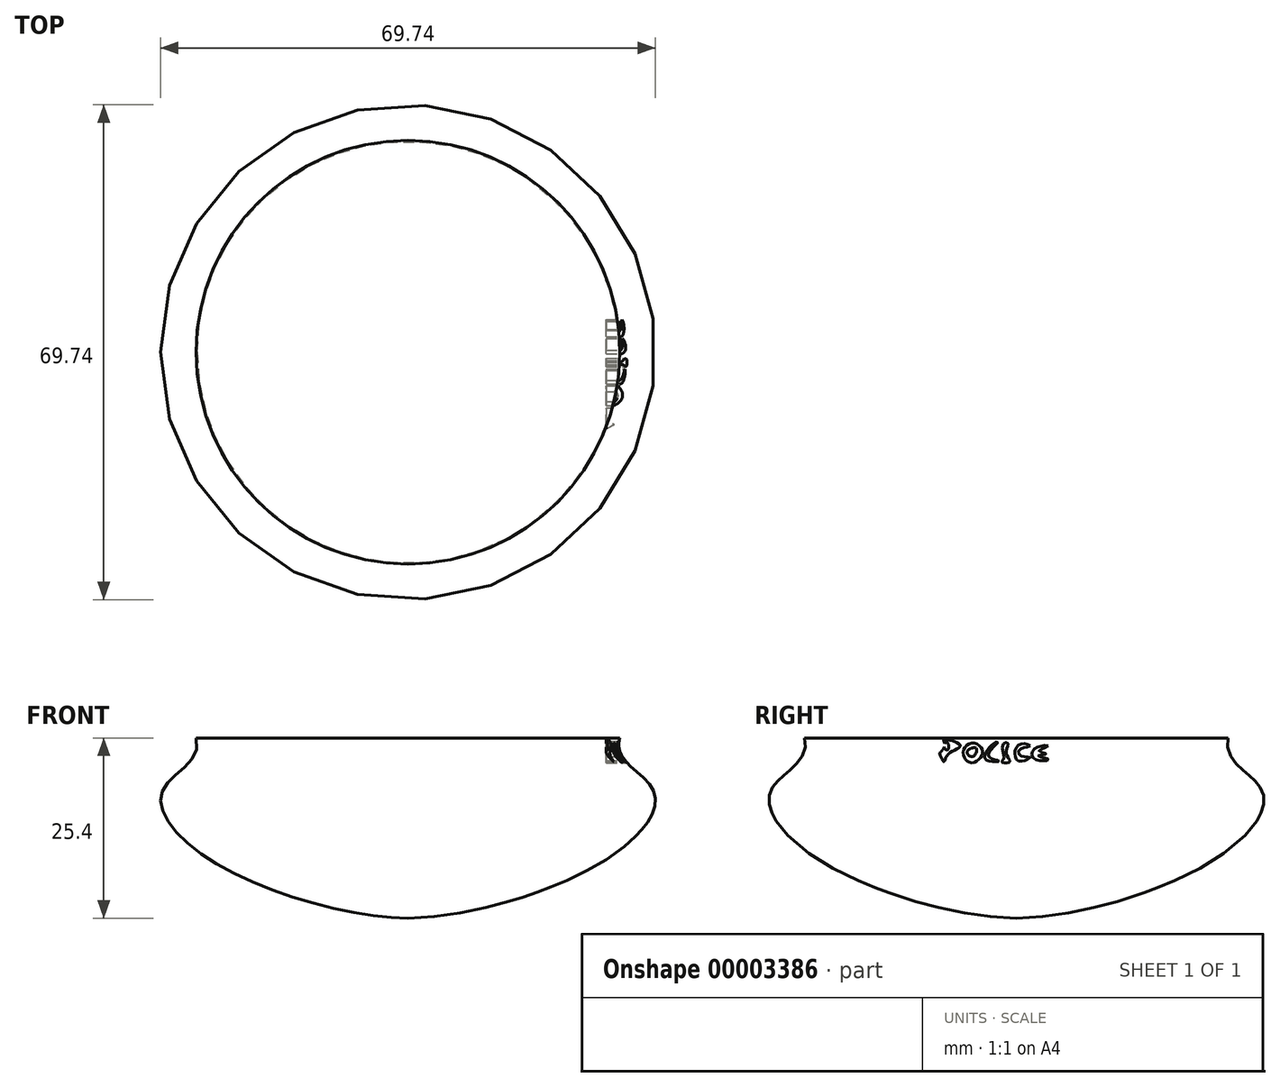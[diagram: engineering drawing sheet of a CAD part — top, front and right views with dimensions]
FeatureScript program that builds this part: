
annotation { "Feature Type Name" : "Feature", "Feature Type Description" : "" }
export const myFeature = defineFeature(function(context is Context, id is Id, definition is map)
    precondition{}
    {
        {
            var Q0;
            Q0=qCreatedBy(makeId("Front.planeOp"),FACE);
            var sketch = newSketch(context, id + "F0", { "sketchPlane" : qUnion([Q0])});
            skFitSpline(sketch, "E0", {"points": [v(-29.85, 0) * mm, v(-34.49, -7.2) * mm, v(-28.54, -16.76) * mm, v(0, -25.4) * mm], "startDerivative": vector(11.46, -40.51) * mm, "endDerivative": vector(51.25, -0.05) * mm});
            skLineSegment(sketch, "E1", {"start": v(-29.85, 0) * mm, "end": v(0, 0) * mm});
            skLineSegment(sketch, "E2", {"start": v(0, 0) * mm, "end": v(0, -25.4) * mm});
            skSolve(sketch);
        }
        {
            var Q0;
            Q0=qCreatedBy(makeId("Front.planeOp"),FACE);
            var sketch = newSketch(context, id + "F1", { "sketchPlane" : qUnion([Q0])});
            skLineSegment(sketch, "E3", {"start": v(0, 38.14) * mm, "end": v(0, -46.32) * mm});
            skSolve(sketch);
        }
        {
            var Q0;
            Q0=makeQuery(id+"F0.imprint","IMPRINT",FACE,{"disambiguationData":[TD([[makeQuery(id+"F0.imprint","IMPRINT",EDGE,{"derivedFrom":sQuery(id+"F0.wireOp",EDGE,"E0")}),1.0]])]});
            var Q1;
            {var subQ0=sQuery(id+"F0.wireOp",EDGE,"7daf59d7-36d5-40c3-b46c-32f78c155582");Q1=makeQuery(id+"F0.imprint","IMPRINT",FACE,{"disambiguationData":[TD([[makeQuery(id+"F0.imprint","IMPRINT",EDGE,{"derivedFrom":subQ0}),1.0]])]});}
            var Q2;
            {var subQ1=sQuery(id+"F0.wireOp",EDGE,"db690256-2e2c-4568-aae6-5ea2a57716da");Q2=makeQuery(id+"F0.imprint","IMPRINT",FACE,{"disambiguationData":[TD([[makeQuery(id+"F0.imprint","IMPRINT",EDGE,{"derivedFrom":subQ1}),1.0]])]});}
            var Q3;
            Q3=sQuery(id+"F1.wireOp",EDGE,"E3");
            revolve(context, id + "F2", {"entities" : qUnion([Q0, Q1, Q2]), "axis" : qUnion([Q3]), "revolveType" : RevolveType.FULL});
        }
        {
            var Q0;
            Q0=qCreatedBy(makeId("Right.planeOp"),FACE);
            cPlane(context, id + "F3", {"entities" : qUnion([Q0]), "cplaneType" : CPlaneType.OFFSET, "offset" : 27.94 * mm, "width" : 152.4 * mm, "height" : 152.4 * mm});
        }
        {
            var Q0;
            Q0=qCreatedBy(id+"F3.planeOp",FACE);
            var sketch = newSketch(context, id + "F4", { "sketchPlane" : qUnion([Q0])});
            skFitSpline(sketch, "E4", {"points": [v(-10.23, -3.34) * mm, v(-10.74, -0.55) * mm, v(-7.93, -1.06) * mm, v(-9.7, -2.4) * mm, v(-10.23, -3.34) * mm]});
            skFitSpline(sketch, "E5", {"points": [v(-10.23, -1) * mm, v(-9.7, -0.66) * mm, v(-9.7, -1.68) * mm, v(-10.23, -1) * mm]});
            skFitSpline(sketch, "E6", {"points": [v(-6.33, -3.5) * mm, v(-7.5, -2.04) * mm, v(-6.3, -0.72) * mm, v(-4.75, -1.9) * mm, v(-6.33, -3.5) * mm]});
            skFitSpline(sketch, "E7", {"points": [v(-6.55, -2.6) * mm, v(-6.93, -1.9) * mm, v(-5.7, -1.4) * mm, v(-5.85, -2.38) * mm, v(-6.55, -2.6) * mm]});
            skFitSpline(sketch, "E8", {"points": [v(-3.2, -0.77) * mm, v(-4.34, -3) * mm, v(-2.38, -3.26) * mm, v(-3.94, -2.54) * mm, v(-2.57, -0.56) * mm, v(-3.2, -0.77) * mm]});
            skFitSpline(sketch, "E9", {"points": [v(-1.78, -0.77) * mm, v(-1.86, -2.2) * mm, v(-1.78, -2.93) * mm, v(-2.02, -3.43) * mm, v(-0.92, -3.38) * mm, v(-1.43, -2.2) * mm, v(-1.19, -0.77) * mm, v(-1.78, -0.77) * mm]});
            skFitSpline(sketch, "E10", {"points": [v(1.95, -1.1) * mm, v(0.32, -0.99) * mm, v(0.23, -3.21) * mm, v(1.95, -2.73) * mm, v(0.6, -2.54) * mm, v(0.46, -1.63) * mm, v(1.95, -1.1) * mm]});
            skFitSpline(sketch, "E11", {"points": [v(4.46, -1.1) * mm, v(2.52, -1.56) * mm, v(2.64, -3.02) * mm, v(4.56, -3.02) * mm, v(3.05, -2.54) * mm, v(4.32, -2.26) * mm, v(3.2, -1.87) * mm, v(4.46, -1.1) * mm]});
            skSolve(sketch);
        }
        {
            var Q0;
            Q0=makeQuery(id+"F4.imprint","IMPRINT",FACE,{"disambiguationData":[TD([[makeQuery(id+"F4.imprint","IMPRINT",EDGE,{"derivedFrom":sQuery(id+"F4.wireOp",EDGE,"E4")}),-1.0]])]});
            var Q1;
            Q1=makeQuery(id+"F4.imprint","IMPRINT",FACE,{"disambiguationData":[TD([[makeQuery(id+"F4.imprint","IMPRINT",EDGE,{"derivedFrom":sQuery(id+"F4.wireOp",EDGE,"E6")}),-1.0]])]});
            var Q2;
            Q2=makeQuery(id+"F4.imprint","IMPRINT",FACE,{"disambiguationData":[TD([[makeQuery(id+"F4.imprint","IMPRINT",EDGE,{"derivedFrom":sQuery(id+"F4.wireOp",EDGE,"E8")}),1.0]])]});
            var Q3;
            Q3=makeQuery(id+"F4.imprint","IMPRINT",FACE,{"disambiguationData":[TD([[makeQuery(id+"F4.imprint","IMPRINT",EDGE,{"derivedFrom":sQuery(id+"F4.wireOp",EDGE,"E9")}),1.0]])]});
            var Q4;
            Q4=makeQuery(id+"F4.imprint","IMPRINT",FACE,{"disambiguationData":[TD([[makeQuery(id+"F4.imprint","IMPRINT",EDGE,{"derivedFrom":sQuery(id+"F4.wireOp",EDGE,"E10")}),1.0]])]});
            var Q5;
            Q5=makeQuery(id+"F4.imprint","IMPRINT",FACE,{"disambiguationData":[TD([[makeQuery(id+"F4.imprint","IMPRINT",EDGE,{"derivedFrom":sQuery(id+"F4.wireOp",EDGE,"E11")}),1.0]])]});
            var Q6;
            Q6=makeQuery(id+"F2.opRevolve","SWEPT_FACE",FACE,{"disambiguationData":[OSD([sQuery(id+"F0.wireOp",EDGE,"E0")])]});
            extrude(context, id + "F5", {"entities" : qUnion([Q0, Q1, Q2, Q3, Q4, Q5]), "operationType" : NewBodyOperationType.REMOVE, "endBound" : BoundingType.UP_TO_SURFACE, "endBoundEntityFace" : qUnion([Q6]), "depth" : 25.4 * mm});
        }
    });
